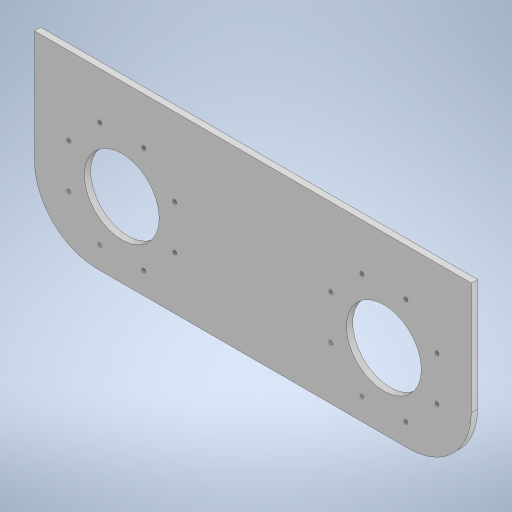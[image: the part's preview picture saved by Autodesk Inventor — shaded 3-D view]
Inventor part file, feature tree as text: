
AUTODESK INVENTOR PART (.ipt)
format: ipt  version: 2024.3 (Build 283343000, 343)  size: 259,584 bytes
history: native  units: mm
features: other x1, extrude x1, fillet x1, sketch x1
ambient origin geometry x8: Origin, YZ Plane, XZ Plane, XY Plane, X Axis, Y Axis, Z Axis, Center Point
bodies: Body1 (feature_tree)
feature tree (4):
  other  "ソリッド1"
  extrude  "押し出し1"  Depth=350.0mm
  fillet  "フィレット2"  Radius=140.0mm
  sketch  "スケッチ1"
